# Revit family: SGD-50
name_source: partatom
category: Lighting Fixtures
units: mm (PartAtom-declared; Revit-internal decimal feet)

## family parameters
Cut with Voids When Loaded = No
Host = Face
Light Source = No
OmniClass Number = 23.80.70.14
OmniClass Title = Luminaries for External Lighting
Part Type = Normal
Room Calculation Point = No
Round Connector Dimension = Use Diameter
Shared = Yes

## types (2) — shared parameters
Apparent Load = 60 VA
Assembly Code = D5020200
Certifications = Listed to UL1598 for use in wet locations
Connector Description = Lighting Connector
Default Elevation = 48 "
Description = SLING FAMILY - DUSK TO DAWN
Features = Multi-purpose dusk-to-dawn LED luminare provides general purpose
area, security, roadway and landscape lighting
• Low profile housing with zero uplight design for environmentally
friendly installations
• Includes arm and photocontrol for automatic off during daylight hours
• Clamp for 1-5/8 inch to 2-3/8 inch diameter pipe
Housing Material = Paint - Metallic Bronze Textured
IP Rating = IP65
Lamp = LED
Length = 48 "
Load Classification = Lighting
Manufacturer = EXO
Model = SGD-50
Pole = Paint - Metallic Bronze Textured
Power Factor = 1
Reflector Finish = White Glass
URL = https://www.currentlighting.com
Voltage = 120 V
Warranty = 5 years Warranty
Wattage Comments = 60W
Watts = 60 W
Width = 11.63 "
Width 1 = 5 "

## per-type parameters (varying)
| type | Head |
| SGD-40-4K | SGD : SGD-40 |
| SGD-60-4K | SGD : SGD-60 |

## geometry (parser evidence)
native form markers: Sweep x7
no freeform markers — native parametric forms only
